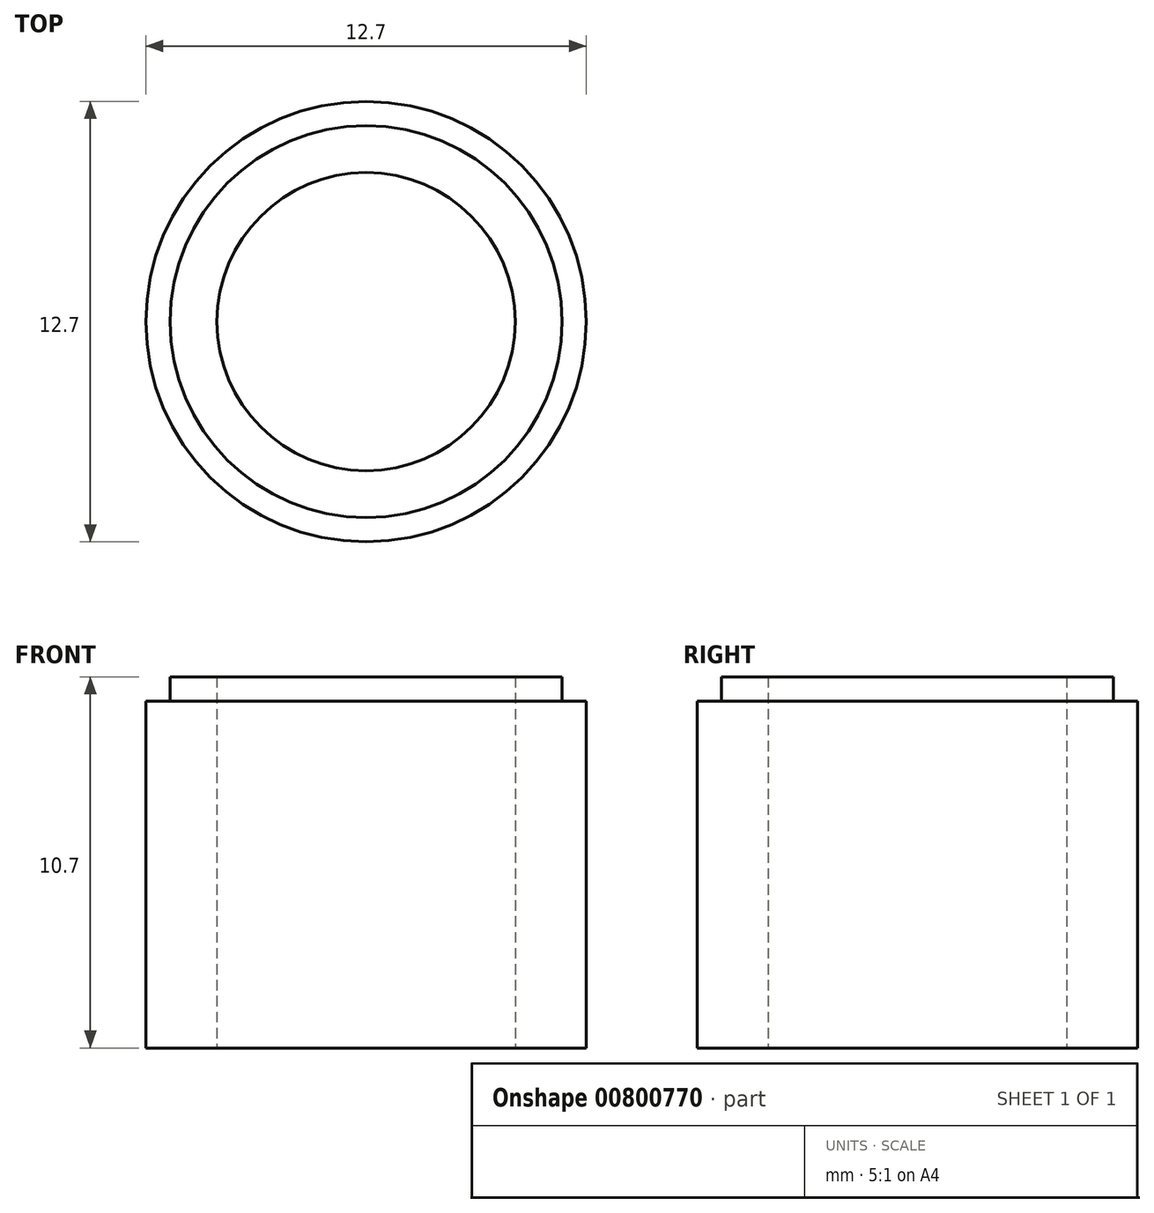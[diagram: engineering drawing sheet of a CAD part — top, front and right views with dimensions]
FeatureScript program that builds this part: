
annotation { "Feature Type Name" : "Feature", "Feature Type Description" : "" }
export const myFeature = defineFeature(function(context is Context, id is Id, definition is map)
    precondition{}
    {
        {
            var Q0;
            Q0=qCreatedBy(makeId("Top.planeOp"),FACE);
            var sketch = newSketch(context, id + "F0", { "sketchPlane" : qUnion([Q0])});
            skCircle(sketch, "E0", {"center": v(0, 0) * mm, "radius": 6.35 * mm});
            skCircle(sketch, "E1", {"center": v(0, 0) * mm, "radius": 5.65 * mm});
            skCircle(sketch, "E2", {"center": v(0, 0) * mm, "radius": 4.3 * mm});
            skSolve(sketch);
        }
        {
            var Q0;
            Q0=makeQuery(id+"F0.imprint","IMPRINT",FACE,{"disambiguationData":[TD([[makeQuery(id+"F0.imprint","IMPRINT",EDGE,{"derivedFrom":sQuery(id+"F0.wireOp",EDGE,"E1")}),1.0]])]});
            extrude(context, id + "F1", {"entities" : qUnion([Q0]), "depth" : .7 * mm, "offsetDistance" : 25 * mm});
        }
        {
            var Q0;
            Q0=makeQuery(id+"F0.imprint","IMPRINT",FACE,{"disambiguationData":[TD([[makeQuery(id+"F0.imprint","IMPRINT",EDGE,{"derivedFrom":sQuery(id+"F0.wireOp",EDGE,"E0")}),1.0]])]});
            var Q1;
            Q1=makeQuery(id+"F0.imprint","IMPRINT",FACE,{"disambiguationData":[TD([[makeQuery(id+"F0.imprint","IMPRINT",EDGE,{"derivedFrom":sQuery(id+"F0.wireOp",EDGE,"E1")}),1.0]])]});
            extrude(context, id + "F2", {"entities" : qUnion([Q0, Q1]), "operationType" : NewBodyOperationType.ADD, "oppositeDirection" : true, "depth" : 10 * mm, "offsetDistance" : 25 * mm});
        }
    });
